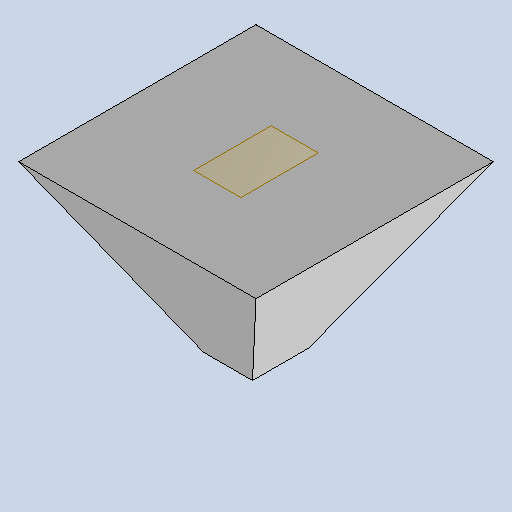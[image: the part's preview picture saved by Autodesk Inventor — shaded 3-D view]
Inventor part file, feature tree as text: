
AUTODESK INVENTOR PART (.ipt)
format: ipt  version: 2025 (Build 290162010, 162A)  size: 97,792 bytes
history: native  units: mm
features: sketch x2, plane x1, loft x1
ambient origin geometry x8: Origin, YZ Plane, XZ Plane, XY Plane, X Axis, Y Axis, Z Axis, Center Point
bodies: Body1 (feature_tree)
feature tree (4):
  sketch  "Sketch2"  dims[d4=1170.0mm d5=0.0mm d6=90.0deg]
  plane  "Work Plane1"
  loft  "Loft1"
  sketch  "Sketch3"  dims[d7=0.0mm d8=90.0deg d9=400.0mm d11=1700.0mm d16=350.0mm d17=1700.0mm]
